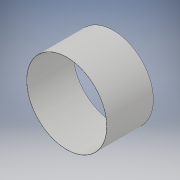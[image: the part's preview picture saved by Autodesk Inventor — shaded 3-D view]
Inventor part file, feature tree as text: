
AUTODESK INVENTOR PART (.ipt)
format: ipt  version: 2019 (Build 230136000, 136)  size: 103,424 bytes
history: native  units: mm
features: extrude x2, sketch x2
ambient origin geometry x8: Origin, YZ Plane, XZ Plane, XY Plane, X Axis, Y Axis, Z Axis, Center Point
bodies: Solid1 (feature_tree)
feature tree (4):
  extrude  "Extrusion1"  Depth=11.68mm TaperAngle=0.0deg
  extrude  "Extrusion2"  Depth=11.68mm TaperAngle=0.0deg
  sketch  "Sketch1"  dims[d0=20.17mm d1=11.68mm d2=0.0mm]
  sketch  "Sketch2"  dims[d3=20.07mm d4=11.68mm d5=0.0mm]
